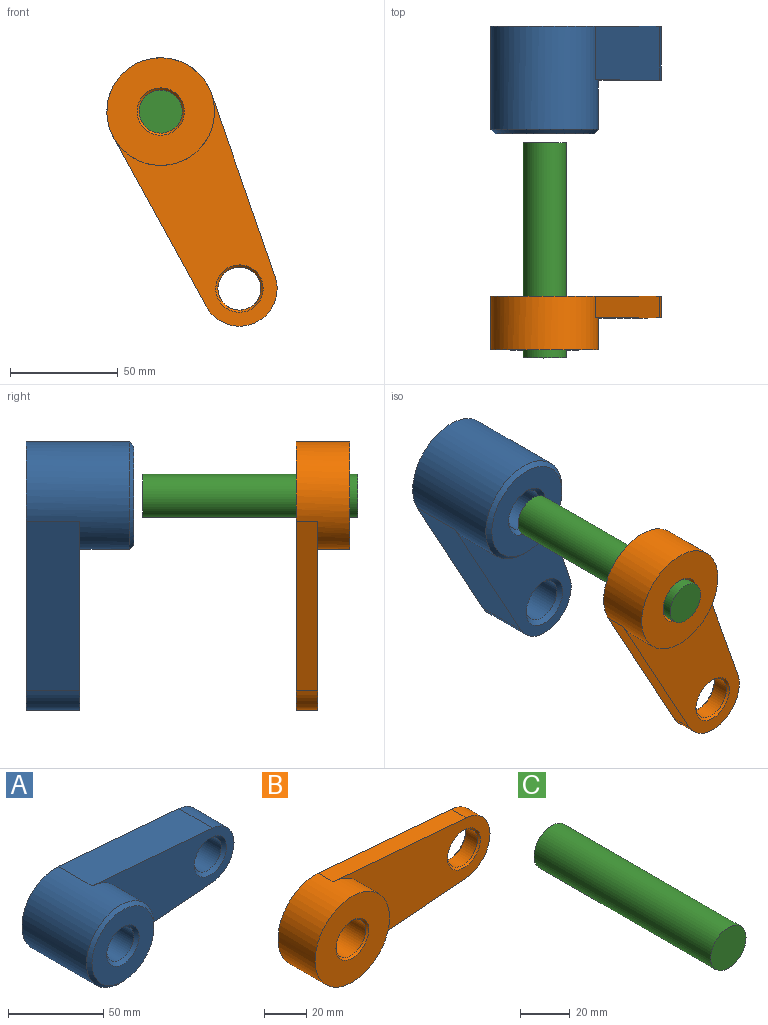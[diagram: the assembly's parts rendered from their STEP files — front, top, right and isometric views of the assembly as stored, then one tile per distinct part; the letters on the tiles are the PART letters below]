
ASSEMBLY  parts=3 mates=2
PART A: 12 faces, bbox 132.5x50x50 mm
  f0: plane 105.42x49.83mm, normal (0,-1,0), area 2885.2mm2, adj f1,f2,f3,f4,f9
  f1: cylinder r=25mm len=50mm, axis (0,1,0), area 5680.6mm2, adj f0,f2,f4,f7,f11
  f2: plane 89.38x25mm, normal (0.08,0,-1), area 2242.2mm2, adj f0,f1,f3,f7
  f3: cylinder r=17.5mm len=34.88mm, axis (0,1,0), area 1301.4mm2, adj f0,f2,f4,f7
  f4: plane 89.38x25mm, normal (0.08,0,1), area 2242.2mm2, adj f0,f1,f3,f7
  f5: cylinder r=10mm len=48mm, axis (0,1,0), area 3015.9mm2, adj f7,f10
  f6: cylinder r=10mm len=23mm, axis (0,1,0), area 1445.1mm2, adj f7,f9
  f7: plane 132.5x50mm, normal (0,1,0), area 4672.8mm2, adj f1,f2,f3,f4,f5,f6
  f8: plane 46x46mm, normal (0,-1,0), area 1209.5mm2, adj f10,f11
  f9: cone r=10mm half-angle=45deg, axis (0,-1,0), area 195.5mm2, adj f0,f6
  f10: cone r=10mm half-angle=45deg, axis (0,-1,0), area 195.5mm2, adj f5,f8
  f11: cone r=23mm half-angle=45deg, axis (0,1,0), area 426.5mm2, adj f1,f8
PART B: 13 faces, bbox 132.5x25x50 mm
  f0: plane 105.42x49.83mm, normal (0,-1,0), area 2957.5mm2, adj f1,f2,f3,f4,f11
  f1: cylinder r=25mm len=50mm, axis (0,1,0), area 3183.3mm2, adj f0,f2,f4,f7,f8
  f2: plane 89.38x10mm, normal (0.08,0,-1), area 896.9mm2, adj f0,f1,f3,f7
  f3: cylinder r=17.5mm len=34.88mm, axis (0,1,0), area 520.6mm2, adj f0,f2,f4,f7
  f4: plane 89.38x10mm, normal (0.08,0,1), area 896.9mm2, adj f0,f1,f3,f7
  f5: cylinder r=10mm len=23mm, axis (0,1,0), area 1445.1mm2, adj f10,f12
  f6: cylinder r=10mm len=20mm, axis (0,1,0), area 502.7mm2, adj f9,f11
  f7: plane 132.5x50mm, normal (0,1,0), area 4540.8mm2, adj f1,f2,f3,f4,f9,f10
  f8: plane 50x50mm, normal (0,-1,0), area 1583.4mm2, adj f1,f12
  f9: cone r=11mm half-angle=45deg, axis (0,1,0), area 93.3mm2, adj f6,f7
  f10: cone r=11mm half-angle=45deg, axis (0,1,0), area 93.3mm2, adj f5,f7
  f11: cone r=10mm half-angle=45deg, axis (0,-1,0), area 93.3mm2, adj f0,f6
  f12: cone r=10mm half-angle=45deg, axis (0,-1,0), area 93.3mm2, adj f5,f8
PART C: 3 faces, bbox 20x100x20 mm
  f0: cylinder r=10mm len=100mm, axis (0,1,0), area 6283.2mm2, adj f1,f2
  f1: plane 20x20mm, normal (0,-1,0), area 314.2mm2, adj f0
  f2: plane 20x20mm, normal (0,1,0), area 314.2mm2, adj f0
PLACE A rot(axis=(0,1,0),66deg) t=(-57.02,124,134.45)mm
PLACE B rot(axis=(0,1,0),66deg) t=(-57.02,-1.45,134.45)mm
PLACE C rot(axis=(0,1,0),66deg) t=(-57.02,69.82,134.45)mm
MATE slider C.f0 <-> B.f5  axis (0,1,0) through (-57.02,19.82,134.45)mm
MATE slider C.f0 <-> A.f1  axis (0,1,0) through (-57.02,19.82,134.45)mm
